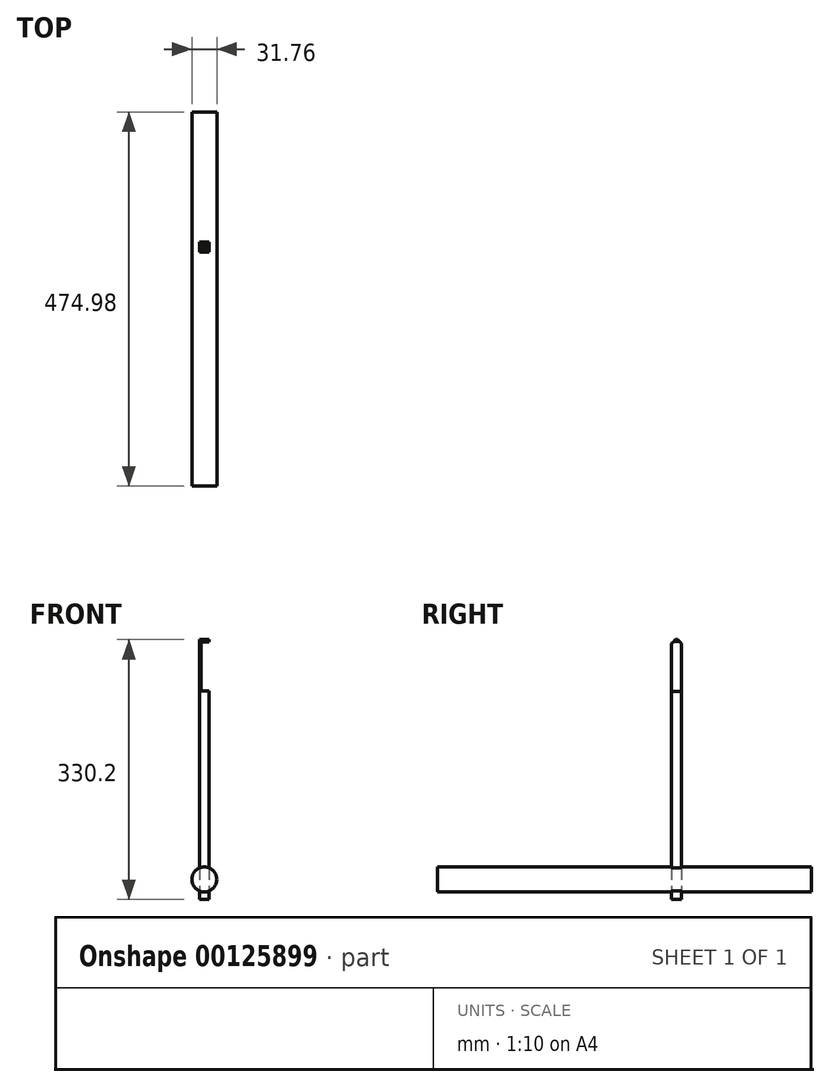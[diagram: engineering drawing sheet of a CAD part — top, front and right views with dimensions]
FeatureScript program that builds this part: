
annotation { "Feature Type Name" : "Feature", "Feature Type Description" : "" }
export const myFeature = defineFeature(function(context is Context, id is Id, definition is map)
    precondition{}
    {
        {
            var Q0;
            Q0=qCreatedBy(makeId("Front.planeOp"),FACE);
            var sketch = newSketch(context, id + "F0", { "sketchPlane" : qUnion([Q0])});
            skCircle(sketch, "E0", {"center": v(0, 0) * mm, "radius": 15.88 * mm});
            skSolve(sketch);
        }
        {
            var Q0;
            Q0=makeQuery(id+"F0.imprint","IMPRINT",FACE,{"disambiguationData":[TD([[makeQuery(id+"F0.imprint","IMPRINT",EDGE,{"derivedFrom":sQuery(id+"F0.wireOp",EDGE,"E0")}),1.0]])]});
            extrude(context, id + "F1", {"entities" : qUnion([Q0]), "depth" : 474.98 * mm});
        }
        {
            var Q0;
            Q0=qCreatedBy(makeId("Top.planeOp"),FACE);
            var sketch = newSketch(context, id + "F2", { "sketchPlane" : qUnion([Q0])});
            skLineSegment(sketch, "E1", {"start": v(0, 0) * mm, "end": v(0, -342.9) * mm, "construction": true});
            skLineSegment(sketch, "E2.bottom", {"start": v(6.35, -165.1) * mm, "end": v(-6.35, -165.1) * mm});
            skLineSegment(sketch, "E2.top", {"start": v(6.35, -177.8) * mm, "end": v(-6.35, -177.8) * mm});
            skLineSegment(sketch, "E2.left", {"start": v(6.35, -165.1) * mm, "end": v(6.35, -177.8) * mm});
            skLineSegment(sketch, "E2.right", {"start": v(-6.35, -165.1) * mm, "end": v(-6.35, -177.8) * mm});
            skPoint(sketch, "E2.middle", {"position": v(0, -171.45) * mm});
            skSolve(sketch);
        }
        {
            var Q0;
            Q0 = qSketchRegion(id + "F2", true);
            extrude(context, id + "F3", {"entities" : qUnion([Q0]), "operationType" : NewBodyOperationType.REMOVE, "endBound" : BoundingType.THROUGH_ALL, "oppositeDirection" : true, "depth" : 25.4 * mm, "hasSecondDirection" : true, "secondDirectionBound" : SecondDirectionBoundingType.THROUGH_ALL, "secondDirectionOppositeDirection" : false, "secondDirectionDepth" : 25.4 * mm});
        }
        {
            var Q0;
            Q0 = qSketchRegion(id + "F2", true);
            extrude(context, id + "F4", {"entities" : qUnion([Q0]), "depth" : 304.8 * mm, "hasSecondDirection" : true, "secondDirectionOppositeDirection" : true, "secondDirectionDepth" : 25.4 * mm});
        }
        {
            var Q0;
            Q0=makeQuery(id+"F4.opExtrude","SWEPT_FACE",FACE,{"disambiguationData":[OSD([sQuery(id+"F2.wireOp",EDGE,"E2.left")])]});
            var sketch = newSketch(context, id + "F5", { "sketchPlane" : qUnion([Q0])});
            skLineSegment(sketch, "E3", {"start": v(-177.8, 304.8) * mm, "end": v(-171.45, 304.8) * mm, "construction": true});
            skLineSegment(sketch, "E4", {"start": v(-171.45, 304.8) * mm, "end": v(-171.45, 270.51) * mm, "construction": true});
            skCircle(sketch, "E5", {"center": v(-171.45, 270.51) * mm, "radius": 31.75 * mm});
            skSolve(sketch);
        }
        {
            var Q0;
            Q0=makeQuery(id+"F4.opExtrude","CAP_EDGE",EDGE,{"disambiguationData":[OSD([sQuery(id+"F2.wireOp",EDGE,"E2.top")])],"isStart":false});
            var Q1;
            Q1=makeQuery(id+"F4.opExtrude","CAP_EDGE",EDGE,{"disambiguationData":[OSD([sQuery(id+"F2.wireOp",EDGE,"E2.bottom")])],"isStart":false});
            chamfer(context, id + "F6", {"entities" : qUnion([Q0, Q1]), "width" : 5.08 * mm, "tangentPropagation" : true});
        }
        {
            var Q0;
            {var subQ0=sQuery(id+"F5.wireOp",EDGE,"E5");var subQ1=sQuery(id+"F2.wireOp",EDGE,"E2.left");var subQ2=makeQuery(id+"F5.imprint","INTERSECT",VERTEX,{"derivedFrom":[makeQuery(id+"F4.opExtrude","CAP_EDGE",EDGE,{"disambiguationData":[OSD([subQ1])],"isStart":false}),subQ0]});Q0=makeQuery(id+"F5.imprint","IMPRINT",FACE,{"disambiguationData":[TD([[makeQuery(id+"F5.imprint","IMPRINT",EDGE,{"disambiguationData":[TD([[subQ2,1.0]])],"derivedFrom":subQ0}),1.0]])]});}
            extrude(context, id + "F7", {"entities" : qUnion([Q0]), "operationType" : NewBodyOperationType.REMOVE, "oppositeDirection" : true, "depth" : 10.16 * mm});
        }
    });
